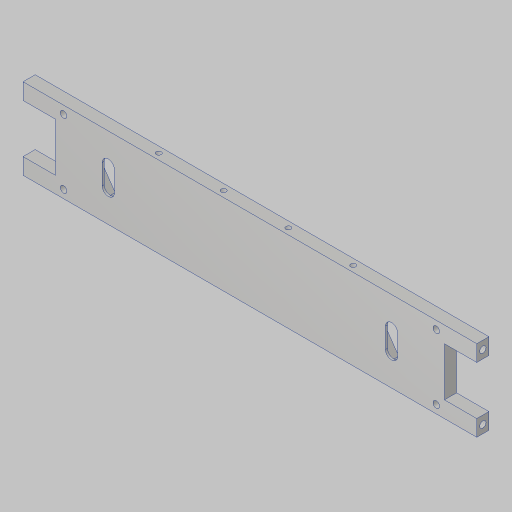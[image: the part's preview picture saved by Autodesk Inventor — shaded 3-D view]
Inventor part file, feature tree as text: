
AUTODESK INVENTOR PART (.ipt)
format: ipt  version: 2023.5 (Build 275446000, 446)  size: 485,888 bytes
history: native  units: in
note: dims shown in document units (in); Inventor stores cm internally (conversion verified against a paired STEP export)
features: sketch x8, extrude x4, hole x4, projected_geometry x3, fillet x1
ambient origin geometry x8: Origin, YZ Plane, XZ Plane, XY Plane, X Axis, Y Axis, Z Axis, Center Point
bodies: Solid1 (feature_tree)
feature tree (20):
  extrude  "Extrusion1"  Depth=2.5in
  hole  "Hole3"  [1 undecoded]
  hole  "Hole4"  [1 undecoded]
  extrude  "Extrusion3"  Depth=0.375in
  extrude  "Extrusion4"  Depth=0.5in
  sketch  "Sketch10"  dims[d49=1.0in d50=1.5in d52=0.5in]
  extrude  "Extrusion5"  Depth=1.5in
  fillet  "Fillet1"  Radius=0.5in
  hole  "Hole6"  [1 undecoded]
  hole  "Hole7"  [1 undecoded]
  sketch  "Sketch1"  dims[d0=14.0in d1=2.5in]
  sketch  "Sketch5"  dims[d2=0.375in d3=0.0in d29=2.0in]
  sketch  "Sketch6"  dims[d30=0.196in d31=0.5in d32=0.385in d33=0.25in d34=0.5635in d35=1.0in d36=0.8108in d37=2.0in]
  sketch  "Sketch8"  dims[d38=0.156in d39=0.38in d40=0.375in d41=0.25in d42=0.5635in d43=0.536in d44=0.8108in d45=1.0in]
  sketch  "Sketch9"  dims[d46=1.5in d47=0.5in]
  projected_geometry  "Projected Loop1"
  projected_geometry  "Projected Loop2"
  sketch  "Sketch11"  dims[d53=1.5625in d54=0.0in d55=0.375in]
  projected_geometry  "Projected Loop3"
  sketch  "Sketch12"  dims[d56=1.0in d57=2.63in d58=0.0in d59=0.0in d60=4.0in d61=2.0in d69=0.25in d72=0.0625in d73=0.0625in d74=0.0625in d75=0.0625in d76=0.0625in d77=0.0625in d78=0.3125in d79=0.0in d80=0.1875in d81=1.6202in d82=0.156in d83=0.38in d84=0.375in d85=0.25in d86=0.5635in d87=1.0in d88=0.8108in d89=1.25in d90=1.25in d91=0.201in d92=0.75in d93=0.385in d94=0.25in d95=0.5635in d96=1.0in d97=0.8108in]
note: 4 required parameter values undecoded (feature->parameter linkage not recoverable at this tier; creation-order binding heuristic only, values carry confidence <= 0.55)
